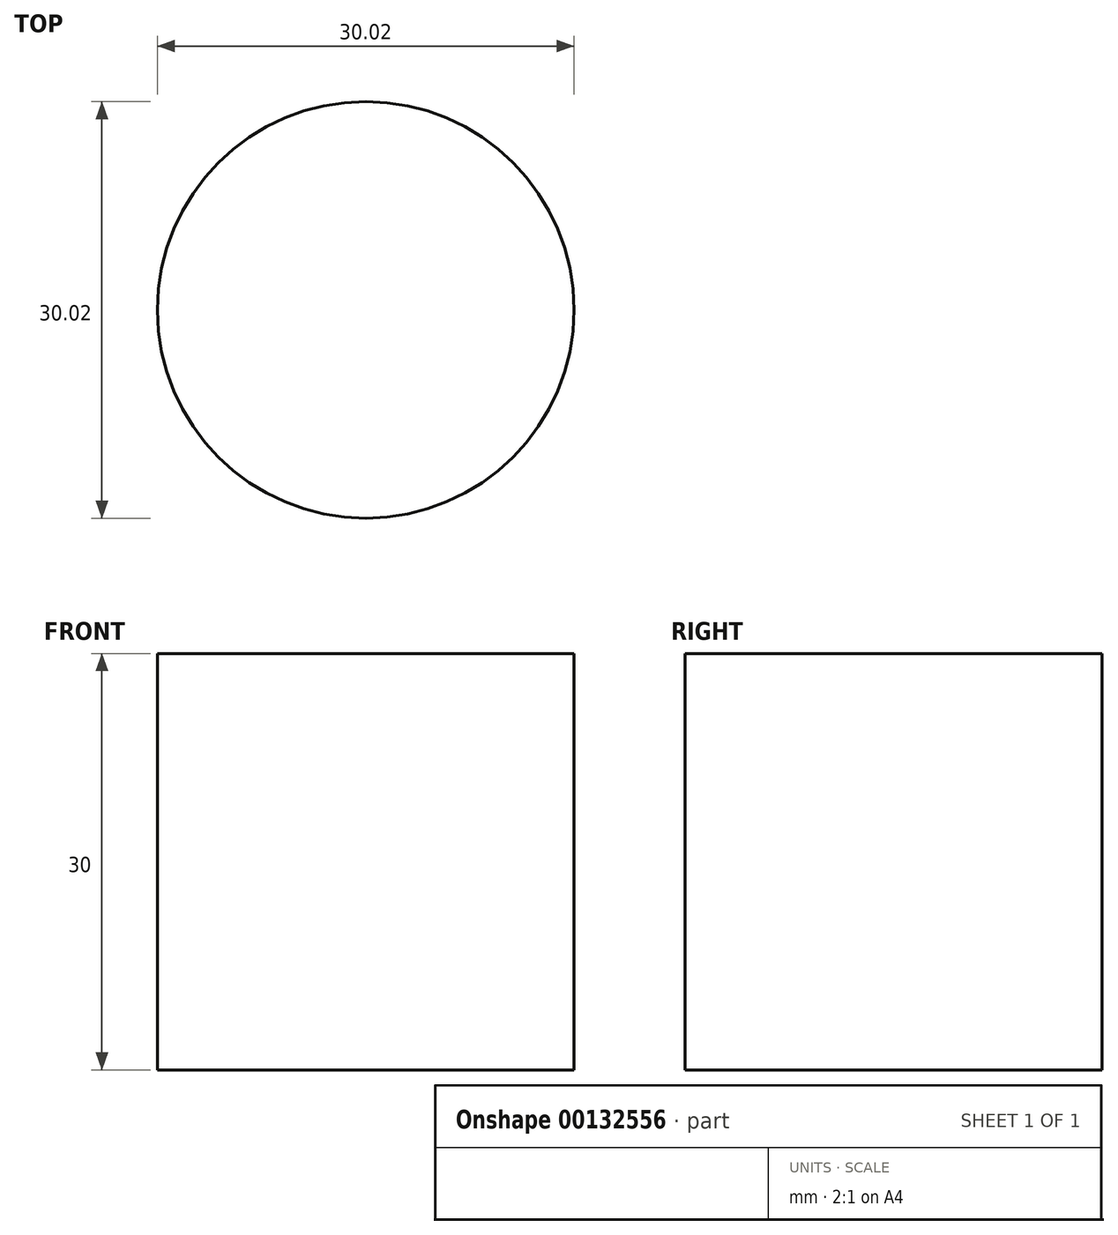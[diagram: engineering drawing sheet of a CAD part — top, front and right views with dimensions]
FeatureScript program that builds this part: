
annotation { "Feature Type Name" : "Feature", "Feature Type Description" : "" }
export const myFeature = defineFeature(function(context is Context, id is Id, definition is map)
    precondition{}
    {
        {
            var Q0;
            Q0=qCreatedBy(makeId("Top.planeOp"),FACE);
            var sketch = newSketch(context, id + "F0", { "sketchPlane" : qUnion([Q0])});
            skCircle(sketch, "E0", {"center": v(0, 0) * mm, "radius": 15 * mm});
            skSolve(sketch);
        }
        {
            var Q0;
            Q0 = qSketchRegion(id + "F0", true);
            extrude(context, id + "F1", {"entities" : qUnion([Q0]), "depth" : 30 * mm});
        }
    });
